FCSTD DOCUMENT  (FreeCAD 0.17R7723 (Git))
Label: FPV49v4
License: All rights reserved
LicenseURL: http://en.wikipedia.org/wiki/All_rights_reserved
objects: Sketcher::SketchObject×4
note: 4 computed .brp shape members not serialized (recipe doc carries the construction recipe); baked Part::Feature solids carry a one-line shape summary decoded from their .brp

FEATURE [Sketcher::SketchObject] Sketch  label="plate A"
  sketch-geometry (10):
    g0: LineSegment StartX=0 StartY=185 StartZ=0 EndX=0 EndY=305 EndZ=0
    g1: LineSegment StartX=0 StartY=305 StartZ=0 EndX=625 EndY=700 EndZ=0
    g2: LineSegment StartX=625 StartY=700 StartZ=0 EndX=625 EndY=505 EndZ=0
    g3: LineSegment StartX=625 StartY=505 StartZ=0 EndX=0 EndY=185 EndZ=0
    g4: LineSegment StartX=-10.6849 StartY=321.907 StartZ=0 EndX=-119.072 EndY=373.406 EndZ=0
    g5: LineSegment StartX=-119.072 StartY=373.406 StartZ=0 EndX=438.185 EndY=800.593 EndZ=0
    g6: LineSegment StartX=438.185 StartY=800.593 StartZ=0 EndX=614.315 EndY=716.907 EndZ=0
    g7: LineSegment StartX=614.315 StartY=716.907 StartZ=0 EndX=-10.6849 EndY=321.907 EndZ=0
    g8: LineSegment StartX=-10.6849 StartY=321.907 StartZ=0 EndX=0 EndY=305 EndZ=0
    g9: LineSegment StartX=614.315 StartY=716.907 StartZ=0 EndX=625 EndY=700 EndZ=0
  constraints (28):
    c: Vertical(g0)
    c: Coincident(g1,g2)
    c: Vertical(g2)
    c: Coincident(g2,g3)
    c: Distance(g2) = 195
    c: Distance(g0) = 120
    c: Distance(g0,g2) = 625
    c: DistanceY(g0,g1) = 395
    c: Coincident(g4,g5)
    c: Coincident(g5,g6)
    c: Coincident(g6,g7)
    c: Coincident(g7,g4)
    c: Coincident(g8,g4)
    c: Coincident(g8,g0)
    c: Coincident(g9,g6)
    c: Coincident(g9,g1)
    c: Equal(g8,g9)
    c: Parallel(g7,g1)
    c: Parallel(g4,g6)
    c: Equal(g6,g2)
    c: Equal(g4,g0)
    c: Distance(g9) = 20
    c: Perpendicular(g1,g8)
    c: Equal(g3,g5)
    c: Coincident(g0,g1)
    c: Coincident(g0,g3)
    c: DistanceX(g0) = 0
    c: DistanceY(g0) = 305
FEATURE [Sketcher::SketchObject] Sketch001  label="plate B"
  sketch-geometry (8):
    g0: LineSegment StartX=0 StartY=125 StartZ=0 EndX=0 EndY=305 EndZ=0
    g1: LineSegment StartX=0 StartY=305 StartZ=0 EndX=625 EndY=700 EndZ=0
    g2: LineSegment StartX=625 StartY=700 StartZ=0 EndX=625 EndY=335 EndZ=0
    g3: LineSegment StartX=625 StartY=335 StartZ=0 EndX=600 EndY=335 EndZ=0
    g4: LineSegment StartX=600 StartY=335 StartZ=0 EndX=560 EndY=326.7 EndZ=0
    g5: LineSegment StartX=560 StartY=378.1 StartZ=0 EndX=0 EndY=125 EndZ=0
    g6: LineSegment StartX=560 StartY=378.1 StartZ=0 EndX=560 EndY=326.7 EndZ=0
    g7: GeomPoint [constr] X=0 Y=305 Z=0
  constraints (22):
    c: Coincident(g0,g1)
    c: Coincident(g1,g2)
    c: Coincident(g2,g3)
    c: Coincident(g3,g4)
    c: Perpendicular(g2,g3)
    c: Distance(g3) = 25
    c: Parallel(g0,g2)
    c: Perpendicular(g-1,g0)
    c: Distance(g2) = 365
    c: Distance(g0,g2) = 625
    c: Coincident(g6,g5)
    c: Coincident(g6,g4)
    c: Parallel(g6,g2)
    c: Distance(g6) = 51.4
    c: Distance(g4,g2) = 65
    c: DistanceY(g4,g1) = 373.3
    c: DistanceY(g0,g1) = 395
    c: Distance(g0) = 180
    c: Coincident(g0,g5)
    c: PointOnObject(g7,g-2)
    c: DistanceY(g7) = 305
    c: Coincident(g0,g7)
FEATURE [Sketcher::SketchObject] Sketch002  label="plate C"
  sketch-geometry (10):
    g0: LineSegment StartX=0 StartY=65 StartZ=0 EndX=0 EndY=305 EndZ=0
    g1: LineSegment StartX=0 StartY=305 StartZ=0 EndX=625 EndY=700 EndZ=0
    g2: LineSegment StartX=625 StartY=700 StartZ=0 EndX=625 EndY=335 EndZ=0
    g3: LineSegment StartX=575 StartY=335 StartZ=0 EndX=457.668 EndY=305 EndZ=0
    g4: LineSegment StartX=457.668 StartY=305 StartZ=0 EndX=447.191 EndY=240.85 EndZ=0
    g5: LineSegment StartX=447.191 StartY=240.85 StartZ=0 EndX=435 EndY=166.211 EndZ=0
    g6: LineSegment StartX=435 StartY=166.211 StartZ=0 EndX=0 EndY=-4.84497 EndZ=0
    g7: LineSegment StartX=0 StartY=-4.84497 StartZ=0 EndX=0 EndY=65 EndZ=0
    g8: LineSegment StartX=0 StartY=65 StartZ=0 EndX=447.191 EndY=240.85 EndZ=0
    g9: LineSegment StartX=625 StartY=335 StartZ=0 EndX=575 EndY=335 EndZ=0
  constraints (29):
    c: Coincident(g1,g2)
    c: Coincident(g3,g4)
    c: Coincident(g4,g5)
    c: Coincident(g5,g6)
    c: Coincident(g6,g7)
    c: Coincident(g7,g0)
    c: Distance(g2,g3) = 170
    c: Distance(g0,g2) = 625
    c: Coincident(g8,g0)
    c: Coincident(g8,g4)
    c: Parallel(g6,g8)
    c: Coincident(g2,g9)
    c: DistanceY(g3,g2) = 30
    c: Perpendicular(g2,g9)
    c: Coincident(g0,g1)
    c: Coincident(g3,g9)
    c: Distance(g9) = 50
    c: Parallel(g4,g5)
    c: Parallel(g7,g0)
    c: Distance(g2) = 365
    c: Distance(g0) = 240
    c: DistanceY(g0,g1) = 395
    c: DistanceX(g-1,g5) = 435
    c: Parallel(g0,g-2)
    c: Parallel(g2,g0)
    c: Distance(g4) = 65
    c: Distance(g0,g6) = 65
    c: DistanceX(g0) = 0
    c: DistanceY(g0) = 305
FEATURE [Sketcher::SketchObject] Sketch003  label="foam board"
  ExternalGeometry = -> [Sketch002]
  MapMode = 2
  Support = -> [Sketch]
  sketch-geometry (4):
    g0: LineSegment StartX=0 StartY=65 StartZ=0 EndX=709.142 EndY=343.858 EndZ=0
    g1: LineSegment StartX=709.142 StartY=343.858 StartZ=0 EndX=523.237 EndY=816.619 EndZ=0
    g2: LineSegment StartX=523.237 StartY=816.619 StartZ=0 EndX=-185.905 EndY=537.761 EndZ=0
    g3: LineSegment StartX=-185.905 StartY=537.761 StartZ=0 EndX=0 EndY=65 EndZ=0
  constraints (11):
    c: Coincident(g0,g1)
    c: Coincident(g1,g2)
    c: Coincident(g2,g3)
    c: Coincident(g3,g0)
    c: Distance(g2) = 762
    c: Distance(g3) = 508
    c: Parallel(g2,g0)
    c: Parallel(g3,g1)
    c: Perpendicular(g0,g1)
    c: Parallel(g0,g-3)
    c: Coincident(g0,g-3)
